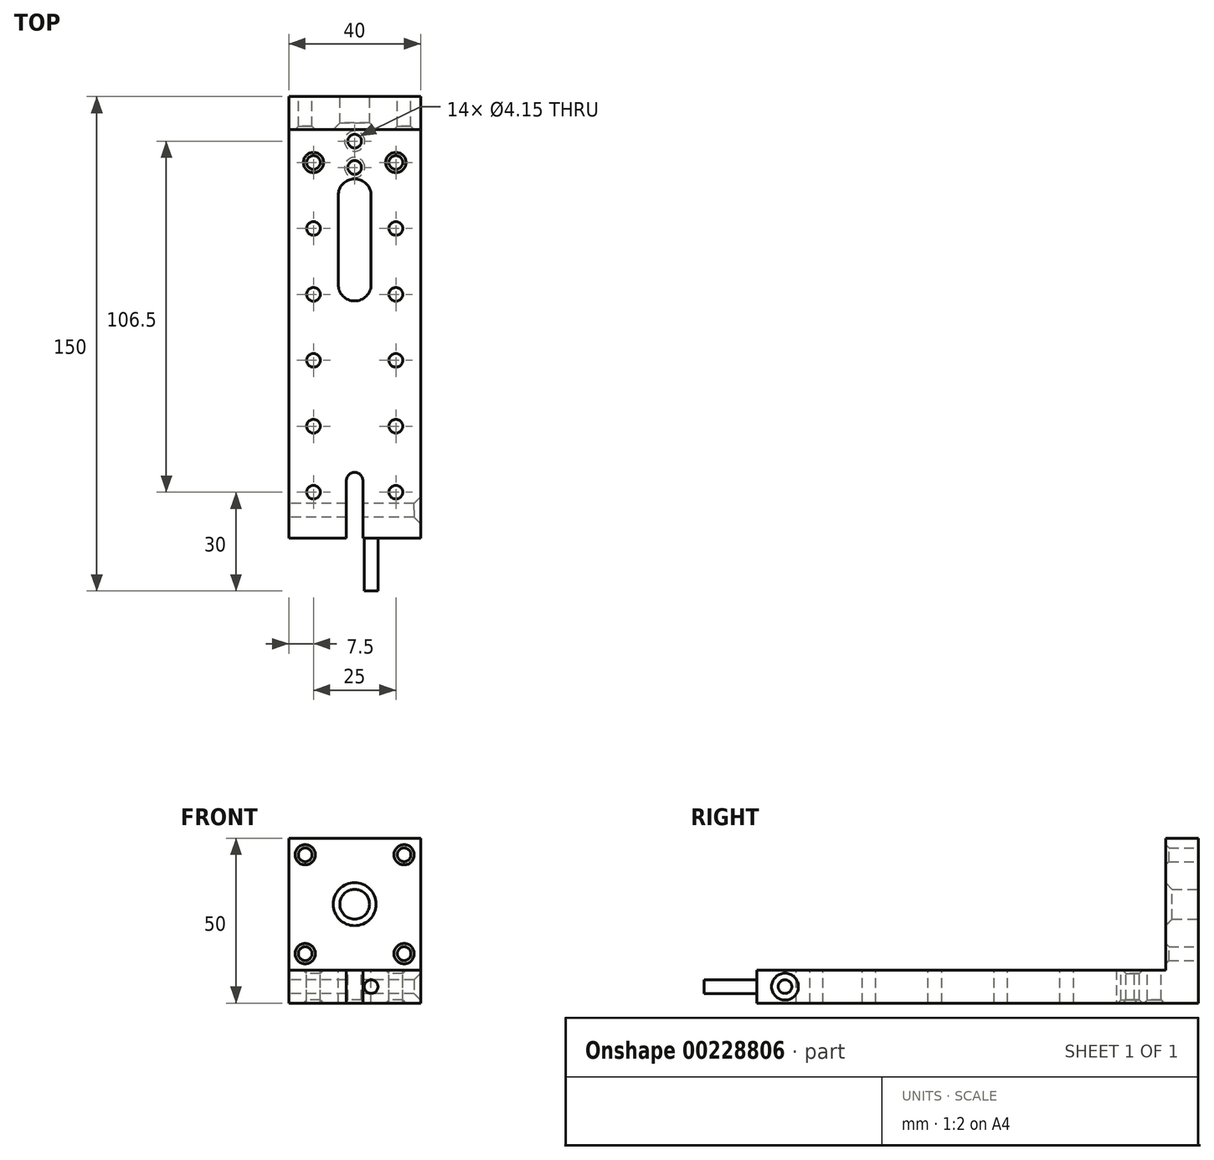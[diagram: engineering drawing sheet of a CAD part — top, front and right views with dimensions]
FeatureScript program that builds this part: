
annotation { "Feature Type Name" : "Feature", "Feature Type Description" : "" }
export const myFeature = defineFeature(function(context is Context, id is Id, definition is map)
    precondition{}
    {
        {
            var Q0;
            Q0=qCreatedBy(makeId("Front.planeOp"),FACE);
            var sketch = newSketch(context, id + "F0", { "sketchPlane" : qUnion([Q0])});
            skCircle(sketch, "E0", {"center": v(0, 0) * mm, "radius": 4.51 * mm});
            skCircle(sketch, "E1", {"center": v(-15, 15) * mm, "radius": 2.07 * mm});
            skCircle(sketch, "E2.1.0", {"center": v(-15, -15) * mm, "radius": 2.07 * mm});
            skCircle(sketch, "E2.2.0", {"center": v(15, -15) * mm, "radius": 2.07 * mm});
            skCircle(sketch, "E2.3.0", {"center": v(15, 15) * mm, "radius": 2.07 * mm});
            skLineSegment(sketch, "E3.bottom", {"start": v(-20, 20) * mm, "end": v(20, 20) * mm});
            skLineSegment(sketch, "E3.top", {"start": v(-20, -30) * mm, "end": v(20, -30) * mm});
            skLineSegment(sketch, "E3.left", {"start": v(-20, 20) * mm, "end": v(-20, -30) * mm});
            skLineSegment(sketch, "E3.right", {"start": v(20, 20) * mm, "end": v(20, -30) * mm});
            skSolve(sketch);
        }
        {
            var Q0;
            Q0=makeQuery(id+"F0.imprint","IMPRINT",FACE,{"disambiguationData":[TD([[makeQuery(id+"F0.imprint","IMPRINT",EDGE,{"derivedFrom":sQuery(id+"F0.wireOp",EDGE,"E0")}),-1.0]])]});
            extrude(context, id + "F1", {"entities" : qUnion([Q0]), "depth" : 10 * mm});
        }
        {
            var Q0;
            Q0=makeQuery(id+"F1.opExtrude","CAP_FACE",FACE,{"disambiguationData":[OSD([sQuery(id+"F0.wireOp",EDGE,"E0"),sQuery(id+"F0.wireOp",EDGE,"E1"),sQuery(id+"F0.wireOp",EDGE,"E2.1.0"),sQuery(id+"F0.wireOp",EDGE,"E2.2.0"),sQuery(id+"F0.wireOp",EDGE,"E2.3.0"),sQuery(id+"F0.wireOp",EDGE,"E3.bottom"),sQuery(id+"F0.wireOp",EDGE,"E3.top"),sQuery(id+"F0.wireOp",EDGE,"E3.left"),sQuery(id+"F0.wireOp",EDGE,"E3.right")])],"isStart":false});
            var sketch = newSketch(context, id + "F2", { "sketchPlane" : qUnion([Q0])});
            skLineSegment(sketch, "E4.bottom", {"start": v(-20, -20) * mm, "end": v(20, -20) * mm});
            skLineSegment(sketch, "E4.top", {"start": v(-20, -30) * mm, "end": v(20, -30) * mm});
            skLineSegment(sketch, "E4.left", {"start": v(-20, -20) * mm, "end": v(-20, -30) * mm});
            skLineSegment(sketch, "E4.right", {"start": v(20, -20) * mm, "end": v(20, -30) * mm});
            skSolve(sketch);
        }
        {
            var Q0;
            Q0=makeQuery(id+"F2.imprint","IMPRINT",FACE,{"disambiguationData":[TD([[makeQuery(id+"F2.imprint","IMPRINT",EDGE,{"derivedFrom":sQuery(id+"F2.wireOp",EDGE,"E4.bottom")}),-1.0]])]});
            extrude(context, id + "F3", {"entities" : qUnion([Q0]), "operationType" : NewBodyOperationType.ADD, "depth" : 140 * mm});
        }
        {
            var Q0;
            Q0=makeQuery(id+"F1.opExtrude","CAP_EDGE",EDGE,{"disambiguationData":[OSD([sQuery(id+"F0.wireOp",EDGE,"E1")])],"isStart":false});
            var Q1;
            Q1=makeQuery(id+"F1.opExtrude","CAP_EDGE",EDGE,{"disambiguationData":[OSD([sQuery(id+"F0.wireOp",EDGE,"E2.3.0")])],"isStart":false});
            var Q2;
            Q2=makeQuery(id+"F1.opExtrude","CAP_EDGE",EDGE,{"disambiguationData":[OSD([sQuery(id+"F0.wireOp",EDGE,"E2.2.0")])],"isStart":false});
            var Q3;
            Q3=makeQuery(id+"F1.opExtrude","CAP_EDGE",EDGE,{"disambiguationData":[OSD([sQuery(id+"F0.wireOp",EDGE,"E2.1.0")])],"isStart":false});
            chamfer(context, id + "F4", {"entities" : qUnion([Q0, Q1, Q2, Q3]), "width" : 1 * mm, "tangentPropagation" : true});
        }
        {
            var Q0;
            Q0=makeQuery(id+"F1.opExtrude","CAP_EDGE",EDGE,{"disambiguationData":[OSD([sQuery(id+"F0.wireOp",EDGE,"E0")])],"isStart":false});
            chamfer(context, id + "F5", {"entities" : qUnion([Q0]), "width" : 2 * mm, "tangentPropagation" : true});
        }
        {
            var Q0;
            Q0=makeQuery(id+"F3.opExtrude","SWEPT_FACE",FACE,{"disambiguationData":[OSD([sQuery(id+"F2.wireOp",EDGE,"E4.bottom")])]});
            var sketch = newSketch(context, id + "F6", { "sketchPlane" : qUnion([Q0])});
            skLineSegment(sketch, "E5.bottom", {"start": v(-5, -25) * mm, "end": v(5, -25) * mm});
            skLineSegment(sketch, "E5.top", {"start": v(-5, -62) * mm, "end": v(5, -62) * mm});
            skLineSegment(sketch, "E5.left", {"start": v(-5, -25) * mm, "end": v(-5, -62) * mm});
            skLineSegment(sketch, "E5.right", {"start": v(5, -25) * mm, "end": v(5, -62) * mm});
            skSolve(sketch);
        }
        {
            var Q0;
            Q0=makeQuery(id+"F6.imprint","IMPRINT",FACE,{"disambiguationData":[TD([[makeQuery(id+"F6.imprint","IMPRINT",EDGE,{"derivedFrom":sQuery(id+"F6.wireOp",EDGE,"E5.bottom")}),-1.0]])]});
            var Q1;
            Q1=makeQuery(id+"F3.boolean.opBoolean","MERGE",FACE,{"derivedFrom":[makeQuery(id+"F1.opExtrude","SWEPT_FACE",FACE,{"disambiguationData":[OSD([sQuery(id+"F0.wireOp",EDGE,"E3.top")])]}),makeQuery(id+"F3.opExtrude","SWEPT_FACE",FACE,{"disambiguationData":[OSD([sQuery(id+"F2.wireOp",EDGE,"E4.top")])]})]});
            extrude(context, id + "F7", {"entities" : qUnion([Q0]), "operationType" : NewBodyOperationType.REMOVE, "endBound" : BoundingType.UP_TO_SURFACE, "oppositeDirection" : true, "endBoundEntityFace" : qUnion([Q1]), "depth" : 25 * mm});
        }
        {
            var Q0;
            Q0=makeQuery(id+"F7.boolean.opBoolean","COPY",EDGE,{"derivedFrom":makeQuery(id+"F7.opExtrude","SWEPT_EDGE",EDGE,{"disambiguationData":[OSD([sQuery(id+"F6.wireOp",EDGE,"E5.top"),sQuery(id+"F6.wireOp",EDGE,"E5.right")])]})});
            var Q1;
            Q1=makeQuery(id+"F7.boolean.opBoolean","COPY",EDGE,{"derivedFrom":makeQuery(id+"F7.opExtrude","SWEPT_EDGE",EDGE,{"disambiguationData":[OSD([sQuery(id+"F6.wireOp",EDGE,"E5.top"),sQuery(id+"F6.wireOp",EDGE,"E5.left")])]})});
            var Q2;
            Q2=makeQuery(id+"F7.boolean.opBoolean","COPY",EDGE,{"derivedFrom":makeQuery(id+"F7.opExtrude","SWEPT_EDGE",EDGE,{"disambiguationData":[OSD([sQuery(id+"F6.wireOp",EDGE,"E5.bottom"),sQuery(id+"F6.wireOp",EDGE,"E5.right")])]})});
            var Q3;
            Q3=makeQuery(id+"F7.boolean.opBoolean","COPY",EDGE,{"derivedFrom":makeQuery(id+"F7.opExtrude","SWEPT_EDGE",EDGE,{"disambiguationData":[OSD([sQuery(id+"F6.wireOp",EDGE,"E5.bottom"),sQuery(id+"F6.wireOp",EDGE,"E5.left")])]})});
            fillet(context, id + "F8", {"entities" : qUnion([Q0, Q1, Q2, Q3]), "radius" : 5 * mm, "tangentPropagation" : true, "allowEdgeOverflow" : false});
        }
        {
            var Q0;
            Q0=makeQuery(id+"F3.opExtrude","SWEPT_FACE",FACE,{"disambiguationData":[OSD([sQuery(id+"F2.wireOp",EDGE,"E4.bottom")])]});
            var sketch = newSketch(context, id + "F9", { "sketchPlane" : qUnion([Q0])});
            skCircle(sketch, "E6", {"center": v(-12.5, -140) * mm, "radius": 2.07 * mm});
            skCircle(sketch, "E7.0.1.0", {"center": v(-12.5, -120) * mm, "radius": 2.07 * mm});
            skCircle(sketch, "E7.0.2.0", {"center": v(-12.5, -100) * mm, "radius": 2.07 * mm});
            skCircle(sketch, "E7.0.3.0", {"center": v(-12.5, -80) * mm, "radius": 2.07 * mm});
            skCircle(sketch, "E7.0.4.0", {"center": v(-12.5, -60) * mm, "radius": 2.07 * mm});
            skLineSegment(sketch, "E7.direction1", {"start": v(-12.5, -140) * mm, "end": v(12.5, -140) * mm, "construction": true});
            skLineSegment(sketch, "E7.direction2", {"start": v(-12.5, -140) * mm, "end": v(-12.5, -120) * mm, "construction": true});
            skLineSegment(sketch, "E8.MirrorCS", {"start": v(12.5, -140) * mm, "end": v(-12.5, -140) * mm, "construction": true});
            skLineSegment(sketch, "E9.MirrorCS", {"start": v(12.5, -140) * mm, "end": v(12.5, -120) * mm, "construction": true});
            skCircle(sketch, "E10.MirrorC", {"center": v(12.5, -60) * mm, "radius": 2.07 * mm});
            skCircle(sketch, "E11.MirrorC", {"center": v(12.5, -80) * mm, "radius": 2.07 * mm});
            skCircle(sketch, "E12.MirrorC", {"center": v(12.5, -100) * mm, "radius": 2.07 * mm});
            skCircle(sketch, "E13.MirrorC", {"center": v(12.5, -140) * mm, "radius": 2.07 * mm});
            skCircle(sketch, "E14.MirrorC", {"center": v(12.5, -120) * mm, "radius": 2.07 * mm});
            skCircle(sketch, "E15.0.0.5", {"center": v(-12.5, -40) * mm, "radius": 2.07 * mm});
            skCircle(sketch, "E16.0.0.6", {"center": v(-12.5, -20) * mm, "radius": 2.07 * mm});
            skCircle(sketch, "E17.MirrorC", {"center": v(12.5, -40) * mm, "radius": 2.07 * mm});
            skCircle(sketch, "E18.MirrorC", {"center": v(12.5, -20) * mm, "radius": 2.07 * mm});
            skSolve(sketch);
        }
        {
            var Q0;
            Q0 = qSketchRegion(id + "F9", true);
            var Q1;
            Q1=makeQuery(id+"F3.boolean.opBoolean","MERGE",FACE,{"derivedFrom":[makeQuery(id+"F1.opExtrude","SWEPT_FACE",FACE,{"disambiguationData":[OSD([sQuery(id+"F0.wireOp",EDGE,"E3.top")])]}),makeQuery(id+"F3.opExtrude","SWEPT_FACE",FACE,{"disambiguationData":[OSD([sQuery(id+"F2.wireOp",EDGE,"E4.top")])]})]});
            extrude(context, id + "F10", {"entities" : qUnion([Q0]), "operationType" : NewBodyOperationType.REMOVE, "endBound" : BoundingType.UP_TO_SURFACE, "oppositeDirection" : true, "endBoundEntityFace" : qUnion([Q1]), "depth" : 25 * mm});
        }
        {
            var Q0;
            Q0=makeQuery(id+"F3.opExtrude","SWEPT_FACE",FACE,{"disambiguationData":[OSD([sQuery(id+"F2.wireOp",EDGE,"E4.bottom")])]});
            var sketch = newSketch(context, id + "F11", { "sketchPlane" : qUnion([Q0])});
            skCircle(sketch, "E19", {"center": v(0, -13.5) * mm, "radius": 2.07 * mm});
            skCircle(sketch, "E20", {"center": v(0, -21.5) * mm, "radius": 2.07 * mm});
            skLineSegment(sketch, "E21", {"start": v(0, -13.5) * mm, "end": v(0, -21.5) * mm, "construction": true});
            skSolve(sketch);
        }
        {
            var Q0;
            Q0=makeQuery(id+"F11.imprint","IMPRINT",FACE,{"disambiguationData":[TD([[makeQuery(id+"F11.imprint","IMPRINT",EDGE,{"derivedFrom":sQuery(id+"F11.wireOp",EDGE,"E19")}),1.0]])]});
            var Q1;
            Q1=makeQuery(id+"F11.imprint","IMPRINT",FACE,{"disambiguationData":[TD([[makeQuery(id+"F11.imprint","IMPRINT",EDGE,{"derivedFrom":sQuery(id+"F11.wireOp",EDGE,"E20")}),1.0]])]});
            extrude(context, id + "F12", {"entities" : qUnion([Q0, Q1]), "operationType" : NewBodyOperationType.REMOVE, "endBound" : BoundingType.THROUGH_ALL, "oppositeDirection" : true, "depth" : 25 * mm});
        }
        {
            var Q0;
            Q0=makeQuery(id+"F3.opExtrude","CAP_FACE",FACE,{"disambiguationData":[OSD([sQuery(id+"F2.wireOp",EDGE,"E4.bottom"),sQuery(id+"F2.wireOp",EDGE,"E4.top"),sQuery(id+"F2.wireOp",EDGE,"E4.left"),sQuery(id+"F2.wireOp",EDGE,"E4.right")])],"isStart":false});
            var sketch = newSketch(context, id + "F13", { "sketchPlane" : qUnion([Q0])});
            skCircle(sketch, "E22", {"center": v(-5, -25) * mm, "radius": 2.07 * mm});
            skLineSegment(sketch, "E23", {"start": v(0, -20) * mm, "end": v(0, -30) * mm, "construction": true});
            skPoint(sketch, "E23.startSnap0", {"position": v(0, -20) * mm});
            skCircle(sketch, "E24.MirrorC", {"center": v(5, -25) * mm, "radius": 2.07 * mm});
            skLineSegment(sketch, "E25", {"start": v(0, -25) * mm, "end": v(-5, -25) * mm, "construction": true});
            skPoint(sketch, "E25.startSnap0", {"position": v(0, -25) * mm});
            skSolve(sketch);
        }
        {
            var Q0;
            Q0=makeQuery(id+"F13.imprint","IMPRINT",FACE,{"disambiguationData":[TD([[makeQuery(id+"F13.imprint","IMPRINT",EDGE,{"derivedFrom":sQuery(id+"F13.wireOp",EDGE,"E22")}),1.0]])]});
            var Q1;
            Q1=makeQuery(id+"F13.imprint","IMPRINT",FACE,{"disambiguationData":[TD([[makeQuery(id+"F13.imprint","IMPRINT",EDGE,{"derivedFrom":sQuery(id+"F13.wireOp",EDGE,"E24.MirrorC")}),-1.0]])]});
            extrude(context, id + "F14", {"entities" : qUnion([Q0, Q1]), "operationType" : NewBodyOperationType.REMOVE, "oppositeDirection" : true, "depth" : 16 * mm});
        }
        {
            var Q0;
            Q0=makeQuery(id+"F12.boolean.opBoolean","INTERSECT",EDGE,{"derivedFrom":[makeQuery(id+"F3.boolean.opBoolean","MERGE",FACE,{"derivedFrom":[makeQuery(id+"F1.opExtrude","SWEPT_FACE",FACE,{"disambiguationData":[OSD([sQuery(id+"F0.wireOp",EDGE,"E3.top")])]}),makeQuery(id+"F3.opExtrude","SWEPT_FACE",FACE,{"disambiguationData":[OSD([sQuery(id+"F2.wireOp",EDGE,"E4.top")])]})]}),makeQuery(id+"F12.opExtrude","SWEPT_FACE",FACE,{"disambiguationData":[OSD([sQuery(id+"F11.wireOp",EDGE,"E20")])]})]});
            var Q1;
            Q1=makeQuery(id+"F12.boolean.opBoolean","INTERSECT",EDGE,{"derivedFrom":[makeQuery(id+"F3.boolean.opBoolean","MERGE",FACE,{"derivedFrom":[makeQuery(id+"F1.opExtrude","SWEPT_FACE",FACE,{"disambiguationData":[OSD([sQuery(id+"F0.wireOp",EDGE,"E3.top")])]}),makeQuery(id+"F3.opExtrude","SWEPT_FACE",FACE,{"disambiguationData":[OSD([sQuery(id+"F2.wireOp",EDGE,"E4.top")])]})]}),makeQuery(id+"F12.opExtrude","SWEPT_FACE",FACE,{"disambiguationData":[OSD([sQuery(id+"F11.wireOp",EDGE,"E19")])]})]});
            chamfer(context, id + "F15", {"entities" : qUnion([Q0, Q1]), "width" : 1 * mm, "tangentPropagation" : true});
        }
        {
            var Q0;
            Q0=makeQuery(id+"F10.boolean.opBoolean","COPY",EDGE,{"derivedFrom":makeQuery(id+"F10.opExtrude","CAP_EDGE",EDGE,{"disambiguationData":[OSD([sQuery(id+"F9.wireOp",EDGE,"E6")])],"isStart":true})});
            var Q1;
            Q1=makeQuery(id+"F10.boolean.opBoolean","COPY",EDGE,{"derivedFrom":makeQuery(id+"F10.opExtrude","CAP_EDGE",EDGE,{"disambiguationData":[OSD([sQuery(id+"F9.wireOp",EDGE,"E13.MirrorC")])],"isStart":true})});
            var Q2;
            Q2=makeQuery(id+"F10.boolean.opBoolean","COPY",EDGE,{"derivedFrom":makeQuery(id+"F10.opExtrude","CAP_EDGE",EDGE,{"disambiguationData":[OSD([sQuery(id+"F9.wireOp",EDGE,"E14.MirrorC")])],"isStart":true})});
            var Q3;
            Q3=makeQuery(id+"F10.boolean.opBoolean","COPY",EDGE,{"derivedFrom":makeQuery(id+"F10.opExtrude","CAP_EDGE",EDGE,{"disambiguationData":[OSD([sQuery(id+"F9.wireOp",EDGE,"E7.0.1.0")])],"isStart":true})});
            var Q4;
            Q4=makeQuery(id+"F10.boolean.opBoolean","COPY",EDGE,{"derivedFrom":makeQuery(id+"F10.opExtrude","CAP_EDGE",EDGE,{"disambiguationData":[OSD([sQuery(id+"F9.wireOp",EDGE,"E12.MirrorC")])],"isStart":true})});
            var Q5;
            Q5=makeQuery(id+"F10.boolean.opBoolean","COPY",EDGE,{"derivedFrom":makeQuery(id+"F10.opExtrude","CAP_EDGE",EDGE,{"disambiguationData":[OSD([sQuery(id+"F9.wireOp",EDGE,"E7.0.2.0")])],"isStart":true})});
            var Q6;
            Q6=makeQuery(id+"F10.boolean.opBoolean","COPY",EDGE,{"derivedFrom":makeQuery(id+"F10.opExtrude","CAP_EDGE",EDGE,{"disambiguationData":[OSD([sQuery(id+"F9.wireOp",EDGE,"E11.MirrorC")])],"isStart":true})});
            var Q7;
            Q7=makeQuery(id+"F10.boolean.opBoolean","COPY",EDGE,{"derivedFrom":makeQuery(id+"F10.opExtrude","CAP_EDGE",EDGE,{"disambiguationData":[OSD([sQuery(id+"F9.wireOp",EDGE,"E7.0.3.0")])],"isStart":true})});
            var Q8;
            Q8=makeQuery(id+"F10.boolean.opBoolean","COPY",EDGE,{"derivedFrom":makeQuery(id+"F10.opExtrude","CAP_EDGE",EDGE,{"disambiguationData":[OSD([sQuery(id+"F9.wireOp",EDGE,"E10.MirrorC")])],"isStart":true})});
            var Q9;
            Q9=makeQuery(id+"F10.boolean.opBoolean","COPY",EDGE,{"derivedFrom":makeQuery(id+"F10.opExtrude","CAP_EDGE",EDGE,{"disambiguationData":[OSD([sQuery(id+"F9.wireOp",EDGE,"E7.0.4.0")])],"isStart":true})});
            var Q10;
            Q10=makeQuery(id+"F10.boolean.opBoolean","COPY",EDGE,{"derivedFrom":makeQuery(id+"F10.opExtrude","CAP_EDGE",EDGE,{"disambiguationData":[OSD([sQuery(id+"F9.wireOp",EDGE,"E15.0.0.5")])],"isStart":true})});
            var Q11;
            Q11=makeQuery(id+"F10.boolean.opBoolean","COPY",EDGE,{"derivedFrom":makeQuery(id+"F10.opExtrude","CAP_EDGE",EDGE,{"disambiguationData":[OSD([sQuery(id+"F9.wireOp",EDGE,"E17.MirrorC")])],"isStart":true})});
            var Q12;
            Q12=makeQuery(id+"F10.boolean.opBoolean","COPY",FACE,{"derivedFrom":makeQuery(id+"F10.opExtrude","SWEPT_FACE",FACE,{"disambiguationData":[OSD([sQuery(id+"F9.wireOp",EDGE,"E16.0.0.6")])]})});
            var Q13;
            Q13=makeQuery(id+"F10.boolean.opBoolean","COPY",FACE,{"derivedFrom":makeQuery(id+"F10.opExtrude","SWEPT_FACE",FACE,{"disambiguationData":[OSD([sQuery(id+"F9.wireOp",EDGE,"E18.MirrorC")])]})});
            chamfer(context, id + "F16", {"entities" : qUnion([Q0, Q1, Q2, Q3, Q4, Q5, Q6, Q7, Q8, Q9, Q10, Q11, Q12, Q13]), "width" : 1 * mm, "tangentPropagation" : true});
        }
        {
            var Q0;
            Q0=makeQuery(id+"F3.opExtrude","SWEPT_FACE",FACE,{"disambiguationData":[OSD([sQuery(id+"F2.wireOp",EDGE,"E4.bottom")])]});
            var sketch = newSketch(context, id + "F17", { "sketchPlane" : qUnion([Q0])});
            skLineSegment(sketch, "E26.bottom", {"start": v(-2.5, -114) * mm, "end": v(2.5, -114) * mm});
            skLineSegment(sketch, "E26.top", {"start": v(-2.5, -144) * mm, "end": v(2.5, -144) * mm});
            skLineSegment(sketch, "E26.left", {"start": v(-2.5, -114) * mm, "end": v(-2.5, -144) * mm});
            skLineSegment(sketch, "E26.right", {"start": v(2.5, -114) * mm, "end": v(2.5, -144) * mm});
            skSolve(sketch);
        }
        {
            var Q0;
            Q0=makeQuery(id+"F17.imprint","IMPRINT",FACE,{"disambiguationData":[TD([[makeQuery(id+"F17.imprint","IMPRINT",EDGE,{"derivedFrom":sQuery(id+"F17.wireOp",EDGE,"E26.bottom")}),-1.0]])]});
            extrude(context, id + "F18", {"entities" : qUnion([Q0]), "operationType" : NewBodyOperationType.REMOVE, "endBound" : BoundingType.THROUGH_ALL, "oppositeDirection" : true, "depth" : 25 * mm});
        }
        {
            var Q0;
            Q0=makeQuery(id+"F18.boolean.opBoolean","COPY",EDGE,{"derivedFrom":makeQuery(id+"F18.opExtrude","SWEPT_EDGE",EDGE,{"disambiguationData":[OSD([sQuery(id+"F17.wireOp",EDGE,"E26.top"),sQuery(id+"F17.wireOp",EDGE,"E26.left")])]})});
            var Q1;
            Q1=makeQuery(id+"F18.boolean.opBoolean","COPY",EDGE,{"derivedFrom":makeQuery(id+"F18.opExtrude","SWEPT_EDGE",EDGE,{"disambiguationData":[OSD([sQuery(id+"F17.wireOp",EDGE,"E26.top"),sQuery(id+"F17.wireOp",EDGE,"E26.right")])]})});
            var Q2;
            Q2=makeQuery(id+"F18.boolean.opBoolean","COPY",EDGE,{"derivedFrom":makeQuery(id+"F18.opExtrude","SWEPT_EDGE",EDGE,{"disambiguationData":[OSD([sQuery(id+"F17.wireOp",EDGE,"E26.bottom"),sQuery(id+"F17.wireOp",EDGE,"E26.left")])]})});
            var Q3;
            Q3=makeQuery(id+"F18.boolean.opBoolean","COPY",EDGE,{"derivedFrom":makeQuery(id+"F18.opExtrude","SWEPT_EDGE",EDGE,{"disambiguationData":[OSD([sQuery(id+"F17.wireOp",EDGE,"E26.bottom"),sQuery(id+"F17.wireOp",EDGE,"E26.right")])]})});
            fillet(context, id + "F19", {"entities" : qUnion([Q0, Q1, Q2, Q3]), "radius" : 2.5 * mm, "tangentPropagation" : true, "allowEdgeOverflow" : false});
        }
        {
            var Q0;
            Q0=makeQuery(id+"F3.boolean.opBoolean","MERGE",FACE,{"derivedFrom":[makeQuery(id+"F1.opExtrude","SWEPT_FACE",FACE,{"disambiguationData":[OSD([sQuery(id+"F0.wireOp",EDGE,"E3.left")])]}),makeQuery(id+"F3.opExtrude","SWEPT_FACE",FACE,{"disambiguationData":[OSD([sQuery(id+"F2.wireOp",EDGE,"E4.left")])]})]});
            var sketch = newSketch(context, id + "F20", { "sketchPlane" : qUnion([Q0])});
            skCircle(sketch, "E27", {"center": v(125.5, -25) * mm, "radius": 2.07 * mm});
            skSolve(sketch);
        }
        {
            var Q0;
            {var subQ0=sQuery(id+"F20.wireOp",EDGE,"E27");var subQ1=makeQuery(id+"F3.boolean.opBoolean","MERGE",EDGE,{"derivedFrom":[makeQuery(id+"F1.opExtrude","SWEPT_EDGE",EDGE,{"disambiguationData":[OSD([sQuery(id+"F0.wireOp",EDGE,"E3.top"),sQuery(id+"F0.wireOp",EDGE,"E3.left")])]}),makeQuery(id+"F3.opExtrude","SWEPT_EDGE",EDGE,{"disambiguationData":[OSD([sQuery(id+"F2.wireOp",EDGE,"E4.top"),sQuery(id+"F2.wireOp",EDGE,"E4.left")])]})]});var subQ2=makeQuery(id+"F20.imprint","INTERSECT",VERTEX,{"disambiguationData":[OD(0.0)],"derivedFrom":[subQ1,subQ0]});Q0=makeQuery(id+"F20.imprint","IMPRINT",FACE,{"disambiguationData":[TD([[makeQuery(id+"F20.imprint","IMPRINT",EDGE,{"disambiguationData":[TD([[subQ2,1.0]])],"derivedFrom":subQ0}),1.0]])]});}
            var Q1;
            {var subQ0=sQuery(id+"F20.wireOp",EDGE,"E27");var subQ1=makeQuery(id+"F3.boolean.opBoolean","MERGE",EDGE,{"derivedFrom":[makeQuery(id+"F1.opExtrude","SWEPT_EDGE",EDGE,{"disambiguationData":[OSD([sQuery(id+"F0.wireOp",EDGE,"E3.top"),sQuery(id+"F0.wireOp",EDGE,"E3.left")])]}),makeQuery(id+"F3.opExtrude","SWEPT_EDGE",EDGE,{"disambiguationData":[OSD([sQuery(id+"F2.wireOp",EDGE,"E4.top"),sQuery(id+"F2.wireOp",EDGE,"E4.left")])]})]});var subQ2=makeQuery(id+"F20.imprint","INTERSECT",VERTEX,{"disambiguationData":[OD(0.0)],"derivedFrom":[subQ1,subQ0]});Q1=makeQuery(id+"F20.imprint","IMPRINT",FACE,{"disambiguationData":[TD([[makeQuery(id+"F20.imprint","IMPRINT",EDGE,{"disambiguationData":[TD([[subQ2,-1.0]])],"derivedFrom":subQ0}),1.0]])]});}
            extrude(context, id + "F21", {"entities" : qUnion([Q0, Q1]), "operationType" : NewBodyOperationType.REMOVE, "endBound" : BoundingType.THROUGH_ALL, "oppositeDirection" : true, "depth" : 25 * mm});
        }
        {
            var Q0;
            Q0=makeQuery(id+"F21.boolean.opBoolean","COPY",EDGE,{"derivedFrom":makeQuery(id+"F21.opExtrude","CAP_EDGE",EDGE,{"disambiguationData":[OSD([sQuery(id+"F20.wireOp",EDGE,"E27")])],"isStart":true})});
            var Q1;
            Q1=makeQuery(id+"F21.boolean.opBoolean","INTERSECT",EDGE,{"derivedFrom":[makeQuery(id+"F3.boolean.opBoolean","MERGE",FACE,{"derivedFrom":[makeQuery(id+"F1.opExtrude","SWEPT_FACE",FACE,{"disambiguationData":[OSD([sQuery(id+"F0.wireOp",EDGE,"E3.right")])]}),makeQuery(id+"F3.opExtrude","SWEPT_FACE",FACE,{"disambiguationData":[OSD([sQuery(id+"F2.wireOp",EDGE,"E4.right")])]})]}),makeQuery(id+"F21.opExtrude","SWEPT_FACE",FACE,{"disambiguationData":[OSD([sQuery(id+"F20.wireOp",EDGE,"E27")])]})]});
            chamfer(context, id + "F22", {"entities" : qUnion([Q0, Q1]), "width" : 2 * mm, "tangentPropagation" : true});
        }
    });
